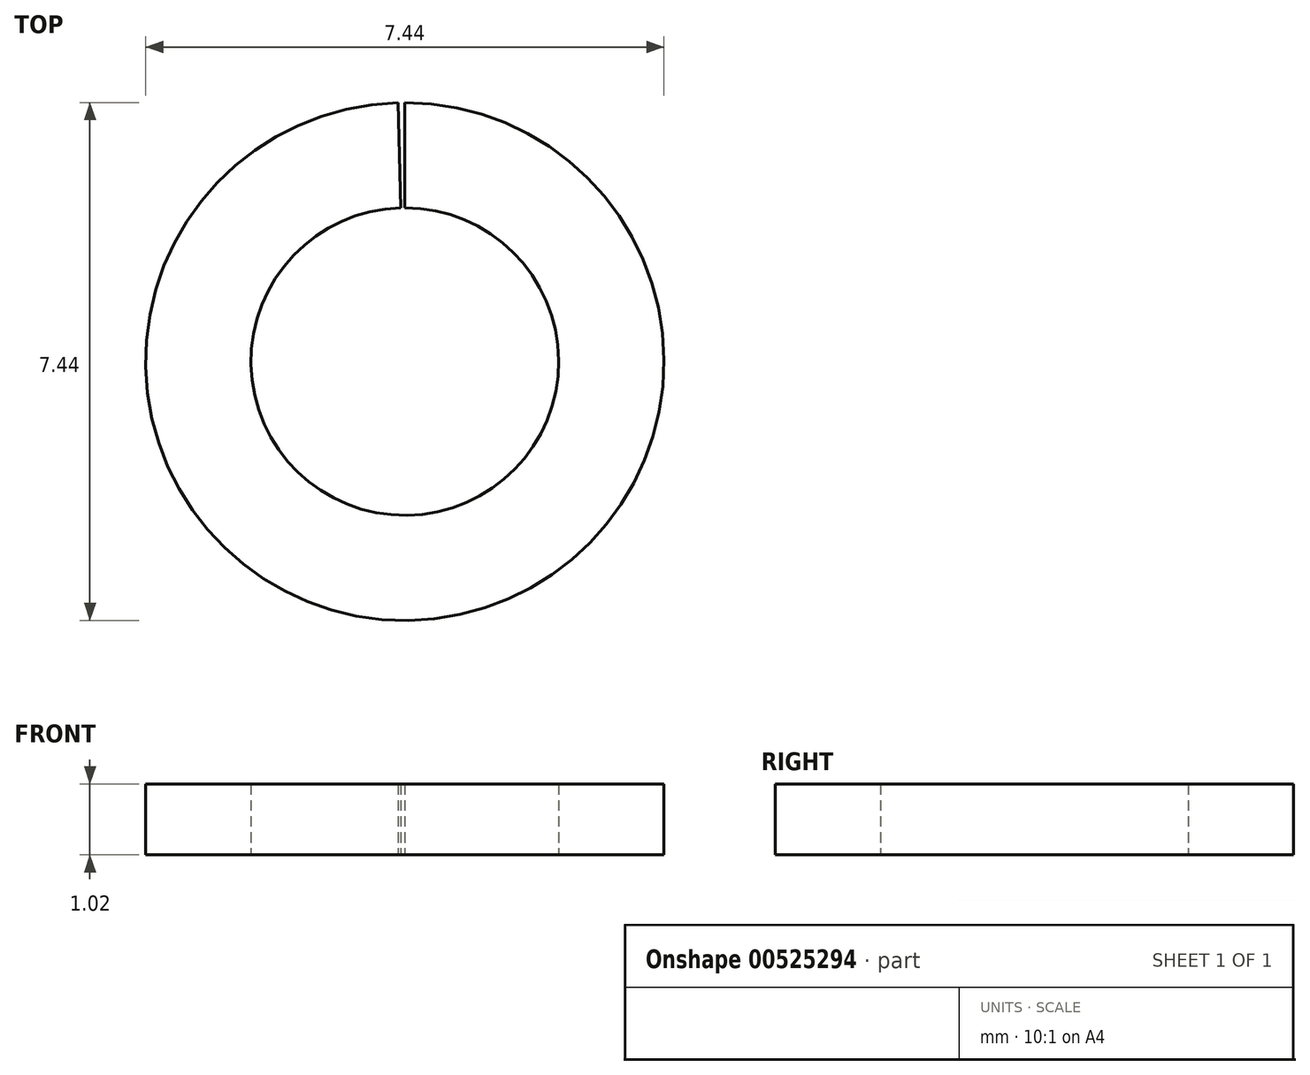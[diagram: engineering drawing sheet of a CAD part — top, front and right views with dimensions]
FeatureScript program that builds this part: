
annotation { "Feature Type Name" : "Feature", "Feature Type Description" : "" }
export const myFeature = defineFeature(function(context is Context, id is Id, definition is map)
    precondition{}
    {
        {
            var Q0;
            Q0=qCreatedBy(makeId("Top.planeOp"),FACE);
            var sketch = newSketch(context, id + "F0", { "sketchPlane" : qUnion([Q0])});
            skArc(sketch, "E0", {"start": v(-0.1, 3.72) * mm, "mid": v(0.05, -3.72) * mm, "end": v(0, 3.72) * mm});
            skArc(sketch, "E1", {"start": v(-0.06, 2.2) * mm, "mid": v(0.03, -2.2) * mm, "end": v(0, 2.2) * mm});
            skLineSegment(sketch, "E2", {"start": v(-0.06, 2.2) * mm, "end": v(-0.1, 3.72) * mm});
            skLineSegment(sketch, "E3", {"start": v(0, 2.2) * mm, "end": v(0, 3.72) * mm});
            skSolve(sketch);
        }
        {
            var Q0;
            Q0=qSketchRegion(id+"F0",true);
            extrude(context, id + "F1", {"entities" : qUnion([Q0]), "depth" : 1.02 * mm, "offsetDistance" : 25.4 * mm});
        }
    });
